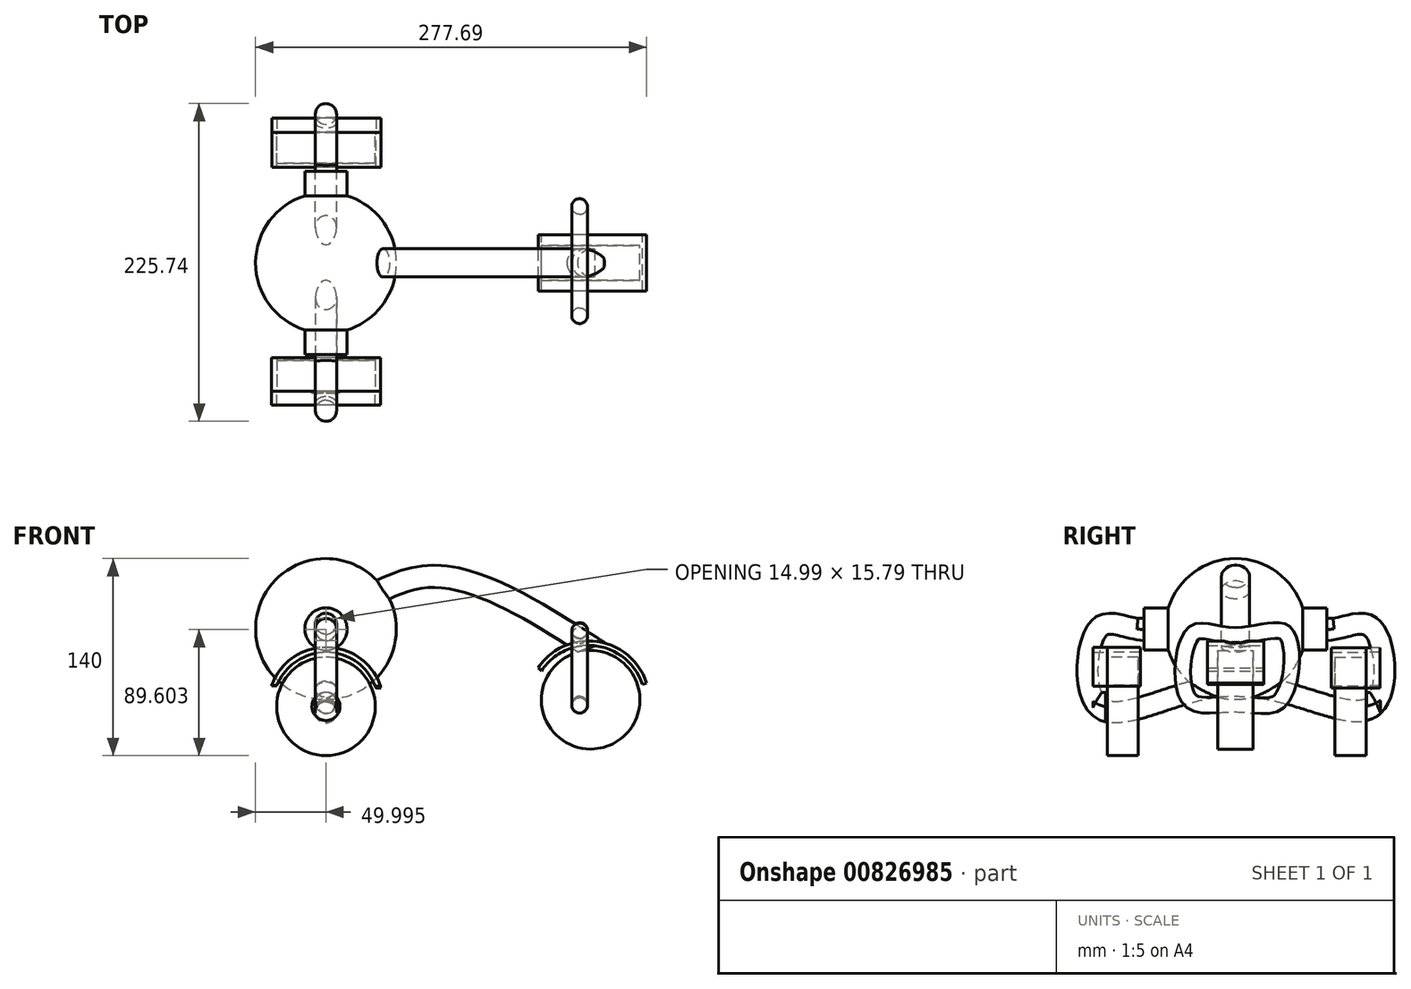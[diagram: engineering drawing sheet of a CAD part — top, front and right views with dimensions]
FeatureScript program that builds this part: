
annotation { "Feature Type Name" : "Feature", "Feature Type Description" : "" }
export const myFeature = defineFeature(function(context is Context, id is Id, definition is map)
    precondition{}
    {
        {
            var Q0;
            Q0=qCreatedBy(makeId("Right.planeOp"),FACE);
            var sketch = newSketch(context, id + "F0", { "sketchPlane" : qUnion([Q0])});
            skArc(sketch, "E0", {"start": v(0, 50) * mm, "mid": v(-50, 0) * mm, "end": v(0, -50) * mm});
            skLineSegment(sketch, "E1", {"start": v(0, 0) * mm, "end": v(0, -50) * mm});
            skLineSegment(sketch, "E2", {"start": v(0, 0) * mm, "end": v(0, 50) * mm});
            skLineSegment(sketch, "E3", {"start": v(0, 0) * mm, "end": v(0, -63.03) * mm, "construction": true});
            skLineSegment(sketch, "E4", {"start": v(0, -63.03) * mm, "end": v(0, 59.12) * mm, "construction": true});
            skSolve(sketch);
        }
        {
            var Q0;
            Q0=makeQuery(id+"F0.imprint","IMPRINT",FACE,{"disambiguationData":[TD([[makeQuery(id+"F0.imprint","IMPRINT",EDGE,{"derivedFrom":sQuery(id+"F0.wireOp",EDGE,"E0")}),1.0]])]});
            var Q1;
            Q1=sQuery(id+"F0.wireOp",EDGE,"E4");
            revolve(context, id + "F1", {"surfaceOperationType" : NewSurfaceOperationType.NEW, "entities" : qUnion([Q0]), "axis" : qUnion([Q1]), "revolveType" : RevolveType.FULL});
        }
        {
            var Q0;
            Q0=qCreatedBy(makeId("Front.planeOp"),FACE);
            var sketch = newSketch(context, id + "F2", { "sketchPlane" : qUnion([Q0])});
            skCircle(sketch, "E5", {"center": v(0, 0) * mm, "radius": 15 * mm});
            skSolve(sketch);
        }
        {
            var Q0;
            Q0 = qSketchRegion(id + "F2", true);
            extrude(context, id + "F3", {"entities" : qUnion([Q0]), "operationType" : NewBodyOperationType.ADD, "endBound" : BoundingType.SYMMETRIC, "depth" : 130 * mm, "offsetDistance" : 25 * mm});
        }
        {
            var Q0;
            Q0=qCreatedBy(makeId("Front.planeOp"),FACE);
            var sketch = newSketch(context, id + "F4", { "sketchPlane" : qUnion([Q0])});
            skCircle(sketch, "E6", {"center": v(0, 0) * mm, "radius": 7.5 * mm});
            skSolve(sketch);
        }
        {
            var Q0;
            Q0 = qSketchRegion(id + "F4", true);
            extrude(context, id + "F5", {"entities" : qUnion([Q0]), "operationType" : NewBodyOperationType.ADD, "endBound" : BoundingType.SYMMETRIC, "depth" : 140 * mm, "offsetDistance" : 25 * mm});
        }
        {
            var Q0;
            Q0=qCreatedBy(makeId("Right.planeOp"),FACE);
            var sketch = newSketch(context, id + "F6", { "sketchPlane" : qUnion([Q0])});
            skFitSpline(sketch, "E7", {"points": [v(0, -40) * mm, v(-97.02, -55.45) * mm, v(-97.67, 0) * mm, v(-70, 0) * mm, v(0, 0) * mm, v(70, 0) * mm, v(97.9, 0) * mm, v(98.1, -54.36) * mm, v(0, -40) * mm]});
            skSolve(sketch);
        }
        {
            var Q0;
            Q0=qCreatedBy(makeId("Front.planeOp"),FACE);
            var sketch = newSketch(context, id + "F7", { "sketchPlane" : qUnion([Q0])});
            skCircle(sketch, "E8", {"center": v(0, 0) * mm, "radius": 7.5 * mm});
            skSolve(sketch);
        }
        {
            var Q0;
            Q0 = qSketchRegion(id + "F7", true);
            var Q1;
            Q1 = qConstructionFilter(qBodyType(qCreatedBy(id + "F6" ,EDGE), BodyType.WIRE), ConstructionObject.NO);
            sweep(context, id + "F8", {"operationType" : NewBodyOperationType.ADD, "profiles" : qUnion([Q0]), "path" : qUnion([Q1])});
        }
        {
            var Q0;
            Q0=qCreatedBy(makeId("Front.planeOp"),FACE);
            cPlane(context, id + "F9", {"entities" : qUnion([Q0]), "cplaneType" : CPlaneType.OFFSET, "offset" : 101.3 * mm, "width" : 150 * mm, "height" : 150 * mm});
        }
        {
            var Q0;
            Q0=qCreatedBy(id+"F9.planeOp",FACE);
            var sketch = newSketch(context, id + "F10", { "sketchPlane" : qUnion([Q0])});
            skCircle(sketch, "E9", {"center": v(0, -52.5) * mm, "radius": 7.5 * mm});
            skSolve(sketch);
        }
        {
            var Q0;
            Q0=qCreatedBy(makeId("Front.planeOp"),FACE);
            cPlane(context, id + "F11", {"entities" : qUnion([Q0]), "cplaneType" : CPlaneType.OFFSET, "offset" : 103.1 * mm, "oppositeDirection" : true, "width" : 150 * mm, "height" : 150 * mm});
        }
        {
            var Q0;
            Q0=qCreatedBy(id+"F11.planeOp",FACE);
            var sketch = newSketch(context, id + "F12", { "sketchPlane" : qUnion([Q0])});
            skCircle(sketch, "E10", {"center": v(0, -52.5) * mm, "radius": 7.5 * mm});
            skSolve(sketch);
        }
        {
            var Q0;
            Q0 = qSketchRegion(id + "F10", true);
            extrude(context, id + "F13", {"entities" : qUnion([Q0]), "operationType" : NewBodyOperationType.ADD, "oppositeDirection" : true, "depth" : 10 * mm, "offsetDistance" : 25 * mm});
        }
        {
            var Q0;
            Q0 = qSketchRegion(id + "F12", true);
            extrude(context, id + "F14", {"entities" : qUnion([Q0]), "operationType" : NewBodyOperationType.ADD, "depth" : 10 * mm, "offsetDistance" : 25 * mm});
        }
        {
            var Q0;
            Q0=qCreatedBy(makeId("Front.planeOp"),FACE);
            cPlane(context, id + "F15", {"entities" : qUnion([Q0]), "cplaneType" : CPlaneType.OFFSET, "offset" : 91.1 * mm, "width" : 150 * mm, "height" : 150 * mm});
        }
        {
            var Q0;
            Q0=qCreatedBy(id+"F15.planeOp",FACE);
            var sketch = newSketch(context, id + "F16", { "sketchPlane" : qUnion([Q0])});
            skCircle(sketch, "E11", {"center": v(0, -55) * mm, "radius": 35 * mm});
            skSolve(sketch);
        }
        {
            var Q0;
            Q0=makeQuery(id+"F16.imprint","IMPRINT",FACE,{"disambiguationData":[TD([[makeQuery(id+"F16.imprint","IMPRINT",EDGE,{"derivedFrom":sQuery(id+"F16.wireOp",EDGE,"E11")}),1.0]])]});
            extrude(context, id + "F17", {"entities" : qUnion([Q0]), "oppositeDirection" : true, "depth" : 22 * mm, "offsetDistance" : 25 * mm});
        }
        {
            var Q0;
            Q0=qCreatedBy(makeId("Front.planeOp"),FACE);
            cPlane(context, id + "F18", {"entities" : qUnion([Q0]), "cplaneType" : CPlaneType.OFFSET, "offset" : 92.7 * mm, "oppositeDirection" : true, "width" : 150 * mm, "height" : 150 * mm});
        }
        {
            var Q0;
            Q0=qCreatedBy(id+"F18.planeOp",FACE);
            var sketch = newSketch(context, id + "F19", { "sketchPlane" : qUnion([Q0])});
            skCircle(sketch, "E12", {"center": v(0, -55) * mm, "radius": 35 * mm});
            skSolve(sketch);
        }
        {
            var Q0;
            Q0=makeQuery(id+"F19.imprint","IMPRINT",FACE,{"disambiguationData":[TD([[makeQuery(id+"F19.imprint","IMPRINT",EDGE,{"derivedFrom":sQuery(id+"F19.wireOp",EDGE,"E12")}),1.0]])]});
            extrude(context, id + "F20", {"entities" : qUnion([Q0]), "depth" : 22 * mm, "offsetDistance" : 25 * mm});
        }
        {
            var Q0;
            Q0=qCreatedBy(makeId("Right.planeOp"),FACE);
            var sketch = newSketch(context, id + "F21", { "sketchPlane" : qUnion([Q0])});
            skCircle(sketch, "E13", {"center": v(0, 0) * mm, "radius": 10 * mm});
            skSolve(sketch);
        }
        {
            var Q0;
            Q0=qCreatedBy(makeId("Front.planeOp"),FACE);
            var sketch = newSketch(context, id + "F22", { "sketchPlane" : qUnion([Q0])});
            skFitSpline(sketch, "E14", {"points": [v(0, 0) * mm, v(75.07, 37.14) * mm, v(188.4, -12.91) * mm], "startDerivative": vector(157.33, 121.45) * mm, "endDerivative": vector(217.53, -138.8) * mm});
            skSolve(sketch);
        }
        {
            var Q0;
            Q0 = qSketchRegion(id + "F21", true);
            var Q1;
            Q1 = qConstructionFilter(qBodyType(qCreatedBy(id + "F22" ,EDGE), BodyType.WIRE), ConstructionObject.NO);
            sweep(context, id + "F23", {"operationType" : NewBodyOperationType.ADD, "profiles" : qUnion([Q0]), "path" : qUnion([Q1])});
        }
        {
            var Q0;
            Q0=qCreatedBy(makeId("Front.planeOp"),FACE);
            var sketch = newSketch(context, id + "F24", { "sketchPlane" : qUnion([Q0])});
            skArc(sketch, "E15", {"start": v(227.69, -38.37) * mm, "mid": v(192.62, -8.88) * mm, "end": v(150.76, -27.5) * mm});
            skArc(sketch, "E16", {"start": v(224.65, -39.42) * mm, "mid": v(191.86, -12.02) * mm, "end": v(153.04, -29.87) * mm});
            skLineSegment(sketch, "E17", {"start": v(150.76, -27.5) * mm, "end": v(153.04, -29.87) * mm});
            skLineSegment(sketch, "E18", {"start": v(224.65, -39.42) * mm, "end": v(227.69, -38.37) * mm});
            skSolve(sketch);
        }
        {
            var Q0;
            Q0=makeQuery(id+"F24.imprint","IMPRINT",FACE,{"disambiguationData":[TD([[makeQuery(id+"F24.imprint","IMPRINT",EDGE,{"derivedFrom":sQuery(id+"F24.wireOp",EDGE,"E15")}),1.0]])]});
            extrude(context, id + "F25", {"entities" : qUnion([Q0]), "operationType" : NewBodyOperationType.ADD, "endBound" : BoundingType.SYMMETRIC, "depth" : 40 * mm, "offsetDistance" : 25 * mm});
        }
        {
            var Q0;
            Q0=qCreatedBy(makeId("Front.planeOp"),FACE);
            var sketch = newSketch(context, id + "F26", { "sketchPlane" : qUnion([Q0])});
            skCircle(sketch, "E19", {"center": v(188, -50.26) * mm, "radius": 35 * mm});
            skSolve(sketch);
        }
        {
            var Q0;
            Q0=makeQuery(id+"F26.imprint","IMPRINT",FACE,{"disambiguationData":[TD([[makeQuery(id+"F26.imprint","IMPRINT",EDGE,{"derivedFrom":sQuery(id+"F26.wireOp",EDGE,"E19")}),1.0]])]});
            extrude(context, id + "F27", {"entities" : qUnion([Q0]), "endBound" : BoundingType.SYMMETRIC, "depth" : 25 * mm, "offsetDistance" : 25 * mm});
        }
        {
            var Q0;
            Q0=qCreatedBy(id+"F15.planeOp",FACE);
            var sketch = newSketch(context, id + "F28", { "sketchPlane" : qUnion([Q0])});
            skArc(sketch, "E20", {"start": v(35.04, -40.78) * mm, "mid": v(0.38, -16.45) * mm, "end": v(-34.77, -40.07) * mm});
            skArc(sketch, "E21", {"start": v(38.83, -40.78) * mm, "mid": v(0.37, -12.87) * mm, "end": v(-38.59, -40.07) * mm});
            skLineSegment(sketch, "E22", {"start": v(-34.77, -40.07) * mm, "end": v(-38.59, -40.07) * mm});
            skLineSegment(sketch, "E23", {"start": v(35.04, -40.78) * mm, "end": v(38.83, -40.78) * mm});
            skSolve(sketch);
        }
        {
            var Q0;
            Q0 = qSketchRegion(id + "F28", true);
            extrude(context, id + "F29", {"entities" : qUnion([Q0]), "oppositeDirection" : true, "depth" : 23.6 * mm, "offsetDistance" : 25 * mm});
        }
        {
            var Q0;
            Q0=makeQuery(id+"F29.opExtrude","CAP_FACE",FACE,{"disambiguationData":[OSD([sQuery(id+"F28.wireOp",EDGE,"E20"),sQuery(id+"F28.wireOp",EDGE,"E21"),sQuery(id+"F28.wireOp",EDGE,"E22"),sQuery(id+"F28.wireOp",EDGE,"E23")])],"isStart":true});
            extrude(context, id + "F30", {"entities" : qUnion([Q0]), "depth" : 10 * mm, "offsetDistance" : 25 * mm});
        }
        {
            var Q0;
            Q0=qCreatedBy(id+"F18.planeOp",FACE);
            var sketch = newSketch(context, id + "F31", { "sketchPlane" : qUnion([Q0])});
            skArc(sketch, "E24", {"start": v(35.49, -41.96) * mm, "mid": v(0.88, -16.66) * mm, "end": v(-34.88, -40.3) * mm});
            skArc(sketch, "E25", {"start": v(38.98, -41.96) * mm, "mid": v(0.87, -13.34) * mm, "end": v(-38.42, -40.3) * mm});
            skLineSegment(sketch, "E26", {"start": v(-38.42, -40.3) * mm, "end": v(-34.88, -40.3) * mm});
            skLineSegment(sketch, "E27", {"start": v(35.49, -41.96) * mm, "end": v(38.98, -41.96) * mm});
            skSolve(sketch);
        }
        {
            var Q0;
            Q0 = qSketchRegion(id + "F31", true);
            extrude(context, id + "F32", {"entities" : qUnion([Q0]), "depth" : 24.7 * mm, "offsetDistance" : 25 * mm});
        }
        {
            var Q0;
            Q0=makeQuery(id+"F32.opExtrude","CAP_FACE",FACE,{"disambiguationData":[OSD([sQuery(id+"F31.wireOp",EDGE,"E24"),sQuery(id+"F31.wireOp",EDGE,"E25"),sQuery(id+"F31.wireOp",EDGE,"E26"),sQuery(id+"F31.wireOp",EDGE,"E27")])],"isStart":true});
            extrude(context, id + "F33", {"entities" : qUnion([Q0]), "depth" : 10 * mm, "offsetDistance" : 25 * mm});
        }
        {
            var Q0;
            Q0=qCreatedBy(id+"F15.planeOp",FACE);
            var sketch = newSketch(context, id + "F34", { "sketchPlane" : qUnion([Q0])});
            skCircle(sketch, "E28", {"center": v(0, -55) * mm, "radius": 10 * mm});
            skSolve(sketch);
        }
        {
            var Q0;
            Q0 = qSketchRegion(id + "F34", true);
            extrude(context, id + "F35", {"entities" : qUnion([Q0]), "depth" : 1.2 * mm, "offsetDistance" : 25 * mm});
        }
        {
            var Q0;
            Q0=qCreatedBy(makeId("Right.planeOp"),FACE);
            cPlane(context, id + "F36", {"entities" : qUnion([Q0]), "cplaneType" : CPlaneType.OFFSET, "offset" : 180 * mm, "width" : 150 * mm, "height" : 150 * mm});
        }
        {
            var Q0;
            Q0=qCreatedBy(id+"F36.planeOp",FACE);
            var sketch = newSketch(context, id + "F37", { "sketchPlane" : qUnion([Q0])});
            skFitSpline(sketch, "E29", {"points": [v(0, 0) * mm, v(-33.38, 0) * mm, v(-36.9, -52.39) * mm, v(0, -57.92) * mm, v(35.52, -53.4) * mm, v(39.04, 0) * mm, v(0, 0) * mm]});
            skSolve(sketch);
        }
        {
            var Q0;
            Q0=qCreatedBy(makeId("Front.planeOp"),FACE);
            var sketch = newSketch(context, id + "F38", { "sketchPlane" : qUnion([Q0])});
            skCircle(sketch, "E30", {"center": v(180.15, -4.64) * mm, "radius": 5.58 * mm});
            skSolve(sketch);
        }
        {
            var Q0;
            Q0 = qSketchRegion(id + "F38", true);
            var Q1;
            Q1 = qConstructionFilter(qBodyType(qCreatedBy(id + "F37" ,EDGE), BodyType.WIRE), ConstructionObject.NO);
            sweep(context, id + "F39", {"profiles" : qUnion([Q0]), "path" : qUnion([Q1])});
        }
    });
